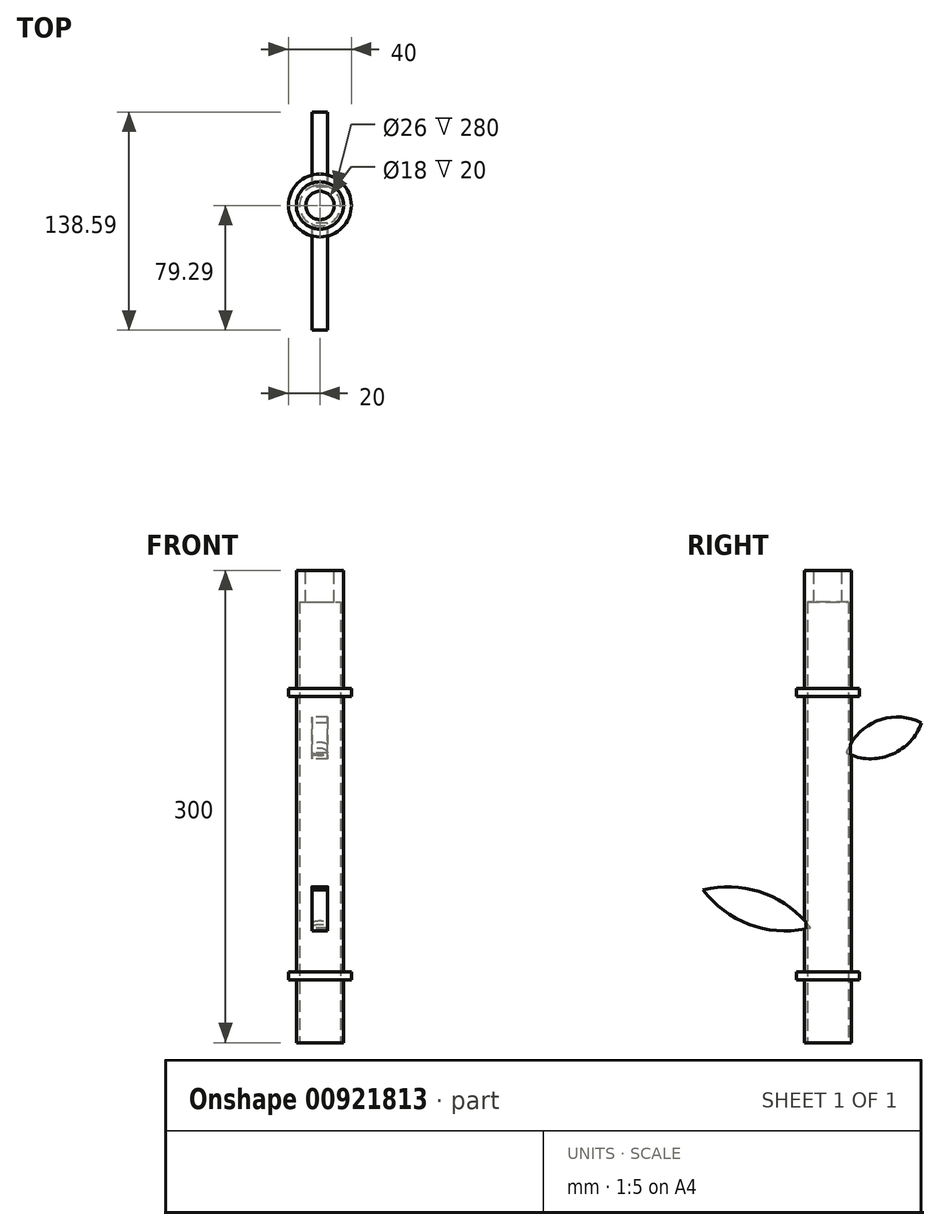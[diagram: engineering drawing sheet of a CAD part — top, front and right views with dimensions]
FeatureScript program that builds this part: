
annotation { "Feature Type Name" : "Feature", "Feature Type Description" : "" }
export const myFeature = defineFeature(function(context is Context, id is Id, definition is map)
    precondition{}
    {
        {
            var Q0;
            Q0=qCreatedBy(makeId("Front.planeOp"),FACE);
            var sketch = newSketch(context, id + "F0", { "sketchPlane" : qUnion([Q0])});
            skLineSegment(sketch, "E0.bottom", {"start": v(0, 116) * mm, "end": v(-15, 116) * mm});
            skLineSegment(sketch, "E0.top", {"start": v(0, -184) * mm, "end": v(-15, -184) * mm});
            skLineSegment(sketch, "E0.left", {"start": v(0, 116) * mm, "end": v(0, -184) * mm});
            skLineSegment(sketch, "E0.right", {"start": v(-15, 116) * mm, "end": v(-15, 41) * mm});
            skLineSegment(sketch, "E1.bottom", {"start": v(-20, 41) * mm, "end": v(-15, 41) * mm});
            skLineSegment(sketch, "E1.top", {"start": v(-20, 36) * mm, "end": v(-15, 36) * mm});
            skLineSegment(sketch, "E1.left", {"start": v(-20, 41) * mm, "end": v(-20, 36) * mm});
            skLineSegment(sketch, "E1.right", {"start": v(0, 41) * mm, "end": v(0, 36) * mm});
            skLineSegment(sketch, "E2.bottom", {"start": v(-20, -139) * mm, "end": v(-15, -139) * mm});
            skLineSegment(sketch, "E2.top", {"start": v(-20, -144) * mm, "end": v(-15, -144) * mm});
            skLineSegment(sketch, "E2.left", {"start": v(-20, -139) * mm, "end": v(-20, -144) * mm});
            skLineSegment(sketch, "E2.right", {"start": v(0, -139) * mm, "end": v(0, -144) * mm});
            skLineSegment(sketch, "E3.trimOffspring", {"start": v(-15, -144) * mm, "end": v(-15, -184) * mm});
            skLineSegment(sketch, "E4.trimOffspring", {"start": v(-15, 36) * mm, "end": v(-15, -139) * mm});
            skSolve(sketch);
        }
        {
            var Q0;
            Q0 = qSketchRegion(id + "F0", true);
            var Q1;
            Q1=sQuery(id+"F0.wireOp",EDGE,"E0.left");
            revolve(context, id + "F1", {"surfaceOperationType" : NewSurfaceOperationType.NEW, "entities" : qUnion([Q0]), "axis" : qUnion([Q1]), "revolveType" : RevolveType.FULL});
        }
        {
            var Q0;
            Q0=makeQuery(id+"F1.opRevolve","SWEPT_FACE",FACE,{"disambiguationData":[OSD([sQuery(id+"F0.wireOp",EDGE,"E0.top")])]});
            var sketch = newSketch(context, id + "F2", { "sketchPlane" : qUnion([Q0])});
            skCircle(sketch, "E5", {"center": v(0, 0) * mm, "radius": 13 * mm});
            skSolve(sketch);
        }
        {
            var Q0;
            Q0=makeQuery(id+"F2.imprint","IMPRINT",FACE,{"disambiguationData":[TD([[makeQuery(id+"F2.imprint","IMPRINT",EDGE,{"derivedFrom":sQuery(id+"F2.wireOp",EDGE,"E5")}),1.0]])]});
            var Q1;
            Q1=sQuery(id+"F2.wireOp",EDGE,"E5");
            extrude(context, id + "F3", {"entities" : qUnion([Q0]), "operationType" : NewBodyOperationType.REMOVE, "surfaceEntities" : qUnion([Q1]), "oppositeDirection" : true, "depth" : 280 * mm, "offsetDistance" : 25 * mm});
        }
        {
            var Q0;
            Q0=makeQuery(id+"F1.opRevolve","SWEPT_FACE",FACE,{"disambiguationData":[OSD([sQuery(id+"F0.wireOp",EDGE,"E0.bottom")])]});
            var sketch = newSketch(context, id + "F4", { "sketchPlane" : qUnion([Q0])});
            skCircle(sketch, "E6", {"center": v(0, 0) * mm, "radius": 9 * mm});
            skSolve(sketch);
        }
        {
            var Q0;
            Q0 = qSketchRegion(id + "F4", true);
            extrude(context, id + "F5", {"entities" : qUnion([Q0]), "operationType" : NewBodyOperationType.REMOVE, "oppositeDirection" : true, "depth" : 25 * mm, "offsetDistance" : 25 * mm});
        }
        {
            var Q0;
            Q0=qCreatedBy(makeId("Right.planeOp"),FACE);
            var sketch = newSketch(context, id + "F6", { "sketchPlane" : qUnion([Q0])});
            skArc(sketch, "E7", {"start": v(59.3, 19.15) * mm, "mid": v(31.19, 20.38) * mm, "end": v(11.78, 0) * mm});
            skArc(sketch, "E8.MirrorCS", {"start": v(59.3, 19.15) * mm, "mid": v(39.9, -1.23) * mm, "end": v(11.78, 0) * mm});
            skArc(sketch, "E9", {"start": v(-79.29, -86.98) * mm, "mid": v(-48.87, -109.29) * mm, "end": v(-11.18, -111.07) * mm});
            skArc(sketch, "E10.MirrorCS", {"start": v(-79.29, -86.98) * mm, "mid": v(-41.6, -88.76) * mm, "end": v(-11.18, -111.07) * mm});
            skSolve(sketch);
        }
        {
            var Q0;
            Q0 = qSketchRegion(id + "F6", true);
            extrude(context, id + "F7", {"entities" : qUnion([Q0]), "operationType" : NewBodyOperationType.ADD, "endBound" : BoundingType.SYMMETRIC, "depth" : 10 * mm, "offsetDistance" : 25 * mm});
        }
    });
